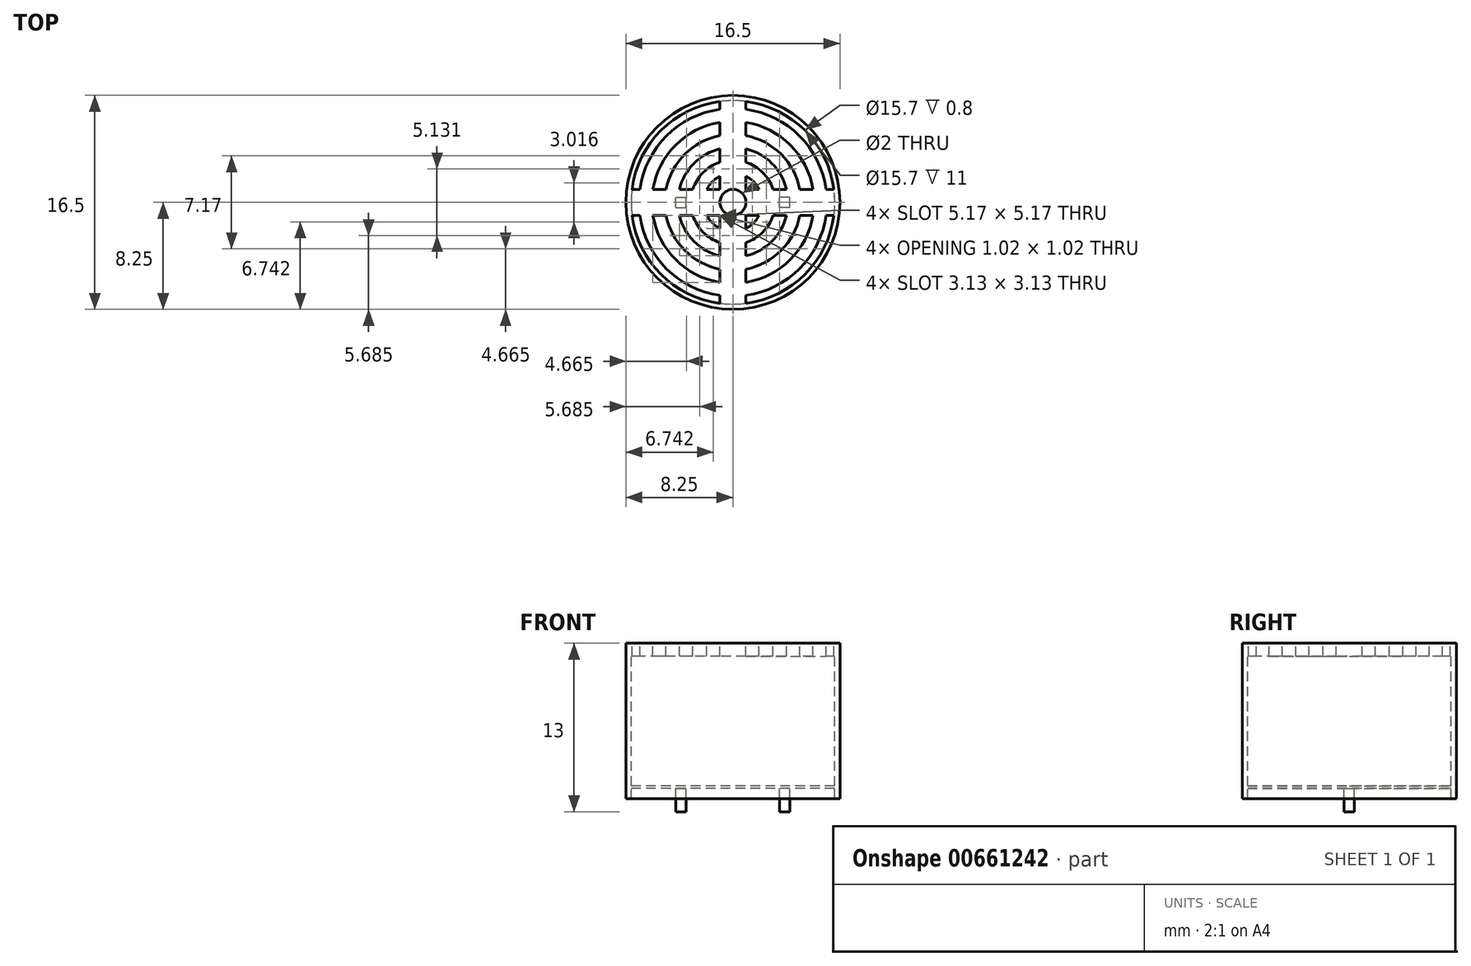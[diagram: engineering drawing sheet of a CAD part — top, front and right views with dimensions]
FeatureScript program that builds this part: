
annotation { "Feature Type Name" : "Feature", "Feature Type Description" : "" }
export const myFeature = defineFeature(function(context is Context, id is Id, definition is map)
    precondition{}
    {
        {
            var Q0;
            Q0=qCreatedBy(makeId("Top.planeOp"),FACE);
            var sketch = newSketch(context, id + "F0", { "sketchPlane" : qUnion([Q0])});
            skCircle(sketch, "E0", {"center": v(0, 0) * mm, "radius": 8.25 * mm});
            skArc(sketch, "E1.0", {"start": v(-1, 7.18) * mm, "mid": v(-5.13, 5.13) * mm, "end": v(-7.18, 1) * mm});
            skArc(sketch, "E2.0", {"start": v(-1, 6.17) * mm, "mid": v(-4.42, 4.42) * mm, "end": v(-6.17, 1) * mm});
            skArc(sketch, "E3.0", {"start": v(-5.15, -1) * mm, "mid": v(-3.71, -3.71) * mm, "end": v(-1, -5.15) * mm});
            skArc(sketch, "E4.0", {"start": v(-4.13, -1) * mm, "mid": v(-3, -3) * mm, "end": v(-1, -4.13) * mm});
            skArc(sketch, "E5.0", {"start": v(-3.1, -1) * mm, "mid": v(-2.3, -2.3) * mm, "end": v(-1, -3.1) * mm});
            skArc(sketch, "E6.0", {"start": v(-2.02, -1) * mm, "mid": v(-1.6, -1.6) * mm, "end": v(-1, -2.02) * mm});
            skCircle(sketch, "E7.0", {"center": v(0, 0) * mm, "radius": 1 * mm});
            skLineSegment(sketch, "E8.bottom", {"start": v(7.79, -1) * mm, "end": v(7.18, -1) * mm});
            skLineSegment(sketch, "E8.top", {"start": v(7.79, 1) * mm, "end": v(7.18, 1) * mm});
            skLineSegment(sketch, "E8.left", {"start": v(8.19, -1) * mm, "end": v(8.19, 1) * mm});
            skLineSegment(sketch, "E8.right", {"start": v(-8.19, -1) * mm, "end": v(-8.19, 1) * mm});
            skLineSegment(sketch, "E9.top", {"start": v(-1, -8.19) * mm, "end": v(1, -8.19) * mm});
            skLineSegment(sketch, "E9.left", {"start": v(-1, 7.79) * mm, "end": v(-1, 7.18) * mm});
            skLineSegment(sketch, "E9.right", {"start": v(1, 7.79) * mm, "end": v(1, 7.18) * mm});
            skLineSegment(sketch, "E10.trimOffspring", {"start": v(1, 6.17) * mm, "end": v(1, 5.15) * mm});
            skLineSegment(sketch, "E11.trimOffspring", {"start": v(-1, 6.17) * mm, "end": v(-1, 5.15) * mm});
            skArc(sketch, "E12.trimOffspring", {"start": v(1, -7.18) * mm, "mid": v(5.13, -5.13) * mm, "end": v(7.18, -1) * mm});
            skLineSegment(sketch, "E13.trimOffspring", {"start": v(-1, -7.18) * mm, "end": v(-1, -7.79) * mm});
            skLineSegment(sketch, "E14.trimOffspring", {"start": v(1, -7.18) * mm, "end": v(1, -7.79) * mm});
            skArc(sketch, "E15.trimOffspring", {"start": v(1, -6.17) * mm, "mid": v(4.42, -4.42) * mm, "end": v(6.17, -1) * mm});
            skArc(sketch, "E16.trimOffspring", {"start": v(-7.18, -1) * mm, "mid": v(-5.13, -5.13) * mm, "end": v(-1, -7.18) * mm});
            skArc(sketch, "E17.trimOffspring", {"start": v(-6.17, -1) * mm, "mid": v(-4.42, -4.42) * mm, "end": v(-1, -6.17) * mm});
            skLineSegment(sketch, "E18.trimOffspring", {"start": v(-7.18, 1) * mm, "end": v(-7.79, 1) * mm});
            skLineSegment(sketch, "E19.trimOffspring", {"start": v(-7.18, -1) * mm, "end": v(-7.79, -1) * mm});
            skLineSegment(sketch, "E20.trimOffspring", {"start": v(6.17, 1) * mm, "end": v(5.15, 1) * mm});
            skArc(sketch, "E21.trimOffspring", {"start": v(6.17, 1) * mm, "mid": v(4.42, 4.42) * mm, "end": v(1, 6.17) * mm});
            skArc(sketch, "E22.trimOffspring", {"start": v(7.18, 1) * mm, "mid": v(5.13, 5.13) * mm, "end": v(1, 7.18) * mm});
            skLineSegment(sketch, "E23.trimOffspring", {"start": v(6.17, -1) * mm, "end": v(5.15, -1) * mm});
            skArc(sketch, "E24.trimOffspring", {"start": v(2.02, 1) * mm, "mid": v(1.6, 1.6) * mm, "end": v(1, 2.02) * mm});
            skArc(sketch, "E25.trimOffspring", {"start": v(3.1, 1) * mm, "mid": v(2.3, 2.3) * mm, "end": v(1, 3.1) * mm});
            skArc(sketch, "E26.trimOffspring", {"start": v(4.13, 1) * mm, "mid": v(3, 3) * mm, "end": v(1, 4.13) * mm});
            skArc(sketch, "E27.trimOffspring", {"start": v(5.15, 1) * mm, "mid": v(3.71, 3.71) * mm, "end": v(1, 5.15) * mm});
            skLineSegment(sketch, "E28.trimOffspring", {"start": v(4.13, 1) * mm, "end": v(3.1, 1) * mm});
            skLineSegment(sketch, "E29.trimOffspring", {"start": v(2.02, 1) * mm, "end": v(1, 1) * mm});
            skLineSegment(sketch, "E30.trimOffspring", {"start": v(-3.1, 1) * mm, "end": v(-4.13, 1) * mm});
            skLineSegment(sketch, "E31.trimOffspring", {"start": v(-5.15, 1) * mm, "end": v(-6.17, 1) * mm});
            skLineSegment(sketch, "E32.trimOffspring", {"start": v(-5.15, -1) * mm, "end": v(-6.17, -1) * mm});
            skLineSegment(sketch, "E33.trimOffspring", {"start": v(-3.1, -1) * mm, "end": v(-4.13, -1) * mm});
            skLineSegment(sketch, "E34.trimOffspring", {"start": v(2.02, -1) * mm, "end": v(1, -1) * mm});
            skLineSegment(sketch, "E35.trimOffspring", {"start": v(4.13, -1) * mm, "end": v(3.1, -1) * mm});
            skLineSegment(sketch, "E36.trimOffspring", {"start": v(1, 4.13) * mm, "end": v(1, 3.1) * mm});
            skLineSegment(sketch, "E37.trimOffspring", {"start": v(-1, 4.13) * mm, "end": v(-1, 3.1) * mm});
            skLineSegment(sketch, "E38.trimOffspring", {"start": v(-1, 2.02) * mm, "end": v(-1, 1) * mm});
            skLineSegment(sketch, "E39.trimOffspring", {"start": v(1, 2.02) * mm, "end": v(1, 1) * mm});
            skLineSegment(sketch, "E40.trimOffspring", {"start": v(1, -3.1) * mm, "end": v(1, -4.13) * mm});
            skLineSegment(sketch, "E41.trimOffspring", {"start": v(-1, -3.1) * mm, "end": v(-1, -4.13) * mm});
            skLineSegment(sketch, "E42.trimOffspring", {"start": v(-1, -5.15) * mm, "end": v(-1, -6.17) * mm});
            skLineSegment(sketch, "E43.trimOffspring", {"start": v(1, -5.15) * mm, "end": v(1, -6.17) * mm});
            skArc(sketch, "E44.trimOffspring", {"start": v(-1, 5.15) * mm, "mid": v(-3.71, 3.71) * mm, "end": v(-5.15, 1) * mm});
            skArc(sketch, "E45.trimOffspring", {"start": v(-1, 4.13) * mm, "mid": v(-3, 3) * mm, "end": v(-4.13, 1) * mm});
            skArc(sketch, "E46.trimOffspring", {"start": v(-1, 3.1) * mm, "mid": v(-2.3, 2.3) * mm, "end": v(-3.1, 1) * mm});
            skArc(sketch, "E47.trimOffspring", {"start": v(-1, 2.02) * mm, "mid": v(-1.6, 1.6) * mm, "end": v(-2.02, 1) * mm});
            skLineSegment(sketch, "E48.trimOffspring", {"start": v(-1, 1) * mm, "end": v(-2.02, 1) * mm});
            skLineSegment(sketch, "E49.trimOffspring", {"start": v(-1, -1) * mm, "end": v(-1, -2.02) * mm});
            skLineSegment(sketch, "E50.trimOffspring", {"start": v(1, -1) * mm, "end": v(1, -2.02) * mm});
            skLineSegment(sketch, "E51.trimOffspring", {"start": v(-1, -1) * mm, "end": v(-2.02, -1) * mm});
            skArc(sketch, "E52.trimOffspring", {"start": v(1, -2.02) * mm, "mid": v(1.6, -1.6) * mm, "end": v(2.02, -1) * mm});
            skArc(sketch, "E53.trimOffspring", {"start": v(1, -3.1) * mm, "mid": v(2.3, -2.3) * mm, "end": v(3.1, -1) * mm});
            skArc(sketch, "E54.trimOffspring", {"start": v(1, -4.13) * mm, "mid": v(3, -3) * mm, "end": v(4.13, -1) * mm});
            skArc(sketch, "E55.trimOffspring", {"start": v(1, -5.15) * mm, "mid": v(3.71, -3.71) * mm, "end": v(5.15, -1) * mm});
            skCircle(sketch, "E56.0", {"center": v(0, 0) * mm, "radius": 7.85 * mm});
            skPoint(sketch, "E57.orphan", {"position": v(-1, 8.19) * mm});
            skPoint(sketch, "E58.orphan", {"position": v(1, 8.19) * mm});
            skSolve(sketch);
        }
        {
            var Q0;
            Q0=qCreatedBy(makeId("Top.planeOp"),FACE);
            cPlane(context, id + "F1", {"entities" : qUnion([Q0]), "cplaneType" : CPlaneType.OFFSET, "offset" : 11 * mm, "oppositeDirection" : true, "width" : 150 * mm, "height" : 150 * mm});
        }
        {
            var Q0;
            Q0=qCreatedBy(id+"F1.planeOp",FACE);
            var sketch = newSketch(context, id + "F2", { "sketchPlane" : qUnion([Q0])});
            skCircle(sketch, "E59.0", {"center": v(0, 0) * mm, "radius": 7.92 * mm});
            skFitSpline(sketch, "E60.0", {"points": [v(3.6, -0.4) * mm, v(3.6, -0.13) * mm, v(3.6, 0.13) * mm, v(3.6, 0.4) * mm]});
            skFitSpline(sketch, "E61.0", {"points": [v(4.4, 0.4) * mm, v(4.13, 0.4) * mm, v(3.87, 0.4) * mm, v(3.6, 0.4) * mm]});
            skFitSpline(sketch, "E62.0", {"points": [v(4.4, -0.4) * mm, v(4.4, -0.13) * mm, v(4.4, 0.13) * mm, v(4.4, 0.4) * mm]});
            skFitSpline(sketch, "E63.0", {"points": [v(4.4, -0.4) * mm, v(4.13, -0.4) * mm, v(3.87, -0.4) * mm, v(3.6, -0.4) * mm]});
            skFitSpline(sketch, "E64.0", {"points": [v(-4.4, -0.4) * mm, v(-4.4, -0.13) * mm, v(-4.4, 0.13) * mm, v(-4.4, 0.4) * mm]});
            skFitSpline(sketch, "E65.0", {"points": [v(-4.4, 0.4) * mm, v(-4.13, 0.4) * mm, v(-3.87, 0.4) * mm, v(-3.6, 0.4) * mm]});
            skFitSpline(sketch, "E66.0", {"points": [v(-3.6, -0.4) * mm, v(-3.6, -0.13) * mm, v(-3.6, 0.13) * mm, v(-3.6, 0.4) * mm]});
            skFitSpline(sketch, "E67.0", {"points": [v(-4.4, -0.4) * mm, v(-4.13, -0.4) * mm, v(-3.87, -0.4) * mm, v(-3.6, -0.4) * mm]});
            skCircle(sketch, "E68.0", {"center": v(0, 0) * mm, "radius": 7.12 * mm});
            skSolve(sketch);
        }
        {
            var Q0;
            Q0=makeQuery(id+"F0.imprint","IMPRINT",FACE,{"disambiguationData":[TD([[makeQuery(id+"F0.imprint","IMPRINT",EDGE,{"derivedFrom":sQuery(id+"F0.wireOp",EDGE,"E1.0")}),1.0]])]});
            extrude(context, id + "F3", {"entities" : qUnion([Q0]), "oppositeDirection" : true, "depth" : 1 * mm, "offsetDistance" : 25 * mm});
        }
        {
            var Q0;
            Q0 = qSketchRegion(id + "F0", true);
            extrude(context, id + "F4", {"entities" : qUnion([Q0]), "operationType" : NewBodyOperationType.ADD, "oppositeDirection" : true, "depth" : 12 * mm, "offsetDistance" : 25 * mm});
        }
        {
            var Q0;
            Q0=makeQuery(id+"F2.imprint","IMPRINT",FACE,{"disambiguationData":[TD([[makeQuery(id+"F2.imprint","IMPRINT",EDGE,{"derivedFrom":sQuery(id+"F2.wireOp",EDGE,"E60.0")}),1.0]])]});
            var Q1;
            Q1=makeQuery(id+"F2.imprint","IMPRINT",FACE,{"disambiguationData":[TD([[makeQuery(id+"F2.imprint","IMPRINT",EDGE,{"derivedFrom":sQuery(id+"F2.wireOp",EDGE,"E59.0")}),1.0]])]});
            extrude(context, id + "F5", {"entities" : qUnion([Q0, Q1]), "operationType" : NewBodyOperationType.ADD, "oppositeDirection" : true, "depth" : 0.2 * mm, "offsetDistance" : 25 * mm});
        }
        {
            var Q0;
            Q0=makeQuery(id+"F2.imprint","IMPRINT",FACE,{"disambiguationData":[TD([[makeQuery(id+"F2.imprint","IMPRINT",EDGE,{"derivedFrom":sQuery(id+"F2.wireOp",EDGE,"E64.0")}),-1.0]])]});
            var Q1;
            Q1=makeQuery(id+"F2.imprint","IMPRINT",FACE,{"disambiguationData":[TD([[makeQuery(id+"F2.imprint","IMPRINT",EDGE,{"derivedFrom":sQuery(id+"F2.wireOp",EDGE,"E60.0")}),-1.0]])]});
            extrude(context, id + "F6", {"entities" : qUnion([Q0, Q1]), "operationType" : NewBodyOperationType.ADD, "oppositeDirection" : true, "depth" : 2 * mm, "offsetDistance" : 25 * mm});
        }
    });
